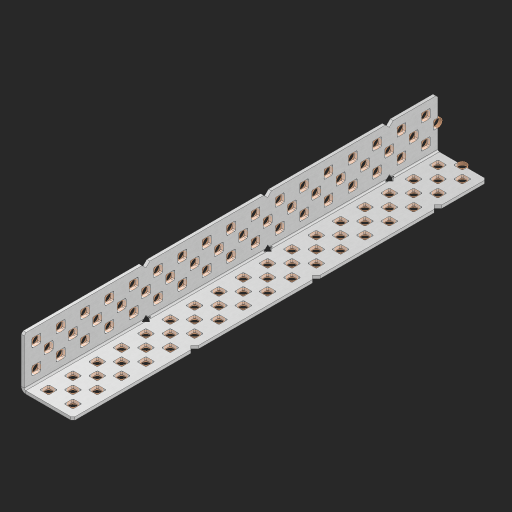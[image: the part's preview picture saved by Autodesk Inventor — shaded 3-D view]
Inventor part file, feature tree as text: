
AUTODESK INVENTOR PART (.ipt)
format: ipt  version: 2023 (Build 270158000, 158)  size: 1,382,912 bytes
history: native  units: in
note: dims shown in document units (in); Inventor stores cm internally (conversion verified against a paired STEP export)
features: other x108, extrude x100, sheet_metal_op x8, sketch x7, pattern_linear x2, mirror x1, chamfer x1
ambient origin geometry x8: Origin, YZ Plane, XZ Plane, XY Plane, X Axis, Y Axis, Z Axis, Center Point
bodies: Solid1 (feature_tree), Body (feature_tree)
feature tree (227):
  sheet_metal_op  "Flanges"
  sheet_metal_op  "Body Pattern"
  pattern_linear  "Center Pattern"  Spacing1=1.0in  [1 undecoded]
  other  "Arc Length"
  pattern_linear  "Notch Pattern"  Spacing1=0.25in  [1 undecoded]
  other  "Diagonal Plane"
  mirror  "Everything Mirrored"
  chamfer  "End Chamfer"
  sketch  "Sketch1"  dims[d0=1.0in]
  other  "Plate1"
  sketch  "Sketch2"  dims[d1=8.5in]
  other  "Plate2"
  sheet_metal_op  "Bend1"
  sheet_metal_op  "Corner1"
  sketch  "Sketch8"  dims[d2=0.0625in]
  sketch  "Sketch9"  dims[d3=0.0625in]
  other  "Srf91"
  sheet_metal_op  "Body Pattern Sketch"
  other  "Srf92"
  sketch  "Sketch13"  dims[d4=0.0312in]
  sketch  "Sketch15"  dims[d5=0.125in]
  sketch  "Sketch16"  dims[d6=0.0625in d7=1.0in d8=90.0deg d9=0.0312in d10=0.25in d11=0.0625in d12=0.0625in d49=0.182in d50=0.02in d52=0.25in d53=0.0625in d54=0.0in d55=0.172in d56=1.0in d57=0.0in d60=6.6929in d62=0.5in d63=0.7874in d65=0.5in d85=0.1473in d86=0.1782in d89=0.0625in d90=0.0in d91=0.04in d92=0.0491in d95=2.5in d96=0.04in d97=0.25in d98=45.0deg d99=0.25in d106=0.182in d107=0.02in d108=0.5in d110=0.0625in d111=0.0in d112=0.172in d113=0.5in d114=0.0in d117=0.5in d123=0.25in d125=0.25in d126=0.0491in d127=0.1473in d128=0.08in d129=0.04in d130=2.5in]
  other  "Srf786"
  other  "Srf856"
  other  "Srf857"
  other  "Srf858"
  other  "Srf859"
  other  "Srf860"
  other  "Srf861"
  other  "Srf889"
  other  "Srf890"
  other  "Srf891"
  other  "Srf1275"
  other  "Srf1276"
  other  "Srf1278"
  other  "Srf1279"
  other  "Srf1280"
  other  "Srf1281"
  other  "Srf1282"
  other  "Srf1283"
  other  "Srf1277"
  other  "Srf1285"
  other  "Srf1286"
  other  "Srf1287"
  other  "Srf1383"
  other  "Srf1384"
  other  "Srf1385"
  other  "Srf1386"
  other  "Srf1387"
  other  "Srf1388"
  other  "Srf1389"
  other  "Srf1390"
  other  "Srf1391"
  other  "Srf1392"
  other  "Srf1393"
  other  "Srf1394"
  other  "Srf1395"
  other  "Srf1396"
  other  "Srf1397"
  other  "Srf1398"
  other  "Srf1399"
  other  "Srf1400"
  other  "Srf1401"
  other  "Srf1402"
  other  "Srf1403"
  other  "Srf1404"
  other  "Srf1405"
  other  "Srf1406"
  other  "Srf1407"
  other  "Srf1408"
  other  "Srf1445"
  other  "Srf1446"
  other  "Srf1447"
  other  "Srf1448"
  other  "Srf1449"
  other  "Srf1450"
  other  "Srf1451"
  other  "Srf1452"
  other  "Srf1453"
  other  "Srf1454"
  other  "Srf1455"
  other  "Srf1456"
  other  "Srf1457"
  other  "Srf1475"
  other  "Srf1476"
  other  "Srf1477"
  other  "Srf1478"
  other  "Srf1479"
  other  "Srf1480"
  other  "Srf1481"
  other  "Srf1482"
  other  "Srf1483"
  other  "Srf1484"
  other  "Srf1485"
  other  "Srf1486"
  other  "Srf1487"
  other  "Srf1488"
  other  "Srf1489"
  other  "Srf1490"
  other  "Srf1491"
  other  "Srf1492"
  other  "Srf1493"
  other  "Srf1494"
  other  "Srf1495"
  other  "Srf1496"
  other  "Srf1497"
  other  "Srf1498"
  other  "Srf1499"
  other  "Srf1500"
  other  "Srf1537"
  other  "Srf1538"
  other  "Srf1539"
  other  "Srf1540"
  other  "Srf1541"
  other  "Srf1542"
  other  "Srf1543"
  other  "Srf1544"
  other  "Srf1545"
  other  "Srf1546"
  other  "Srf1547"
  other  "Srf1548"
  other  "Srf1549"
  sheet_metal_op  "Body Stamp"
  sheet_metal_op  "Body Circle"
  other  "Center Stamp"
  other  "Center Circle"
  sheet_metal_op  "Notch"
  extrude  "ExtrusionSrf92"  Depth=0.0625in
  extrude  "ExtrusionSrf856"  Depth=0.0625in
  extrude  "ExtrusionSrf857"  Depth=0.182in
  extrude  "ExtrusionSrf858"  Depth=0.02in
  extrude  "ExtrusionSrf859"  Depth=0.25in
  extrude  "ExtrusionSrf860"  Depth=0.0625in
  extrude  "ExtrusionSrf861"  TaperAngle=0.0deg  [1 undecoded]
  extrude  "ExtrusionSrf889"  Depth=2.5in
  extrude  "ExtrusionSrf890"  Depth=1.0in TaperAngle=0.0deg
  extrude  "ExtrusionSrf891"  Depth=2.5in
  extrude  "ExtrusionSrf1275"  Depth=0.5in
  extrude  "ExtrusionSrf1276"  Depth=2.5in
  extrude  "ExtrusionSrf1277"  Depth=2.5in
  extrude  "ExtrusionSrf1278"  Depth=0.0625in
  extrude  "ExtrusionSrf1279"  Depth=2.5in TaperAngle=0.0deg
  extrude  "ExtrusionSrf1280"  Depth=2.5in
  extrude  "ExtrusionSrf1281"  Depth=0.25in TaperAngle=45.0deg
  extrude  "ExtrusionSrf1282"  Depth=0.25in
  extrude  "ExtrusionSrf1345"  Depth=0.182in
  extrude  "ExtrusionSrf1346"  Depth=0.02in
  extrude  "ExtrusionSrf1347"  Depth=0.5in
  extrude  "ExtrusionSrf1348"  Depth=0.0625in
  extrude  "ExtrusionSrf1383"  TaperAngle=0.0deg  [1 undecoded]
  extrude  "ExtrusionSrf1384"  Depth=2.5in
  extrude  "ExtrusionSrf1385"  Depth=0.5in TaperAngle=0.0deg
  extrude  "ExtrusionSrf1386"  Depth=0.5in
  extrude  "ExtrusionSrf1387"  Depth=0.25in
  extrude  "ExtrusionSrf1388"  Depth=0.25in
  extrude  "ExtrusionSrf1389"  Depth=2.5in
  extrude  "ExtrusionSrf1390"  Depth=2.5in
  extrude  "ExtrusionSrf1391"  Depth=2.5in
  extrude  "ExtrusionSrf1392"  Depth=2.5in
  extrude  "ExtrusionSrf1393"  Depth=2.5in
  extrude  "ExtrusionSrf1394"  [1 undecoded]
  extrude  "ExtrusionSrf1395"  [1 undecoded]
  extrude  "ExtrusionSrf1396"  [1 undecoded]
  extrude  "ExtrusionSrf1397"  [1 undecoded]
  extrude  "ExtrusionSrf1398"  [1 undecoded]
  extrude  "ExtrusionSrf1399"  [1 undecoded]
  extrude  "ExtrusionSrf1400"  [1 undecoded]
  extrude  "ExtrusionSrf1401"  [1 undecoded]
  extrude  "ExtrusionSrf1402"  [1 undecoded]
  extrude  "ExtrusionSrf1403"  [1 undecoded]
  extrude  "ExtrusionSrf1404"  [1 undecoded]
  extrude  "ExtrusionSrf1405"  [1 undecoded]
  extrude  "ExtrusionSrf1406"  [1 undecoded]
  extrude  "ExtrusionSrf1407"  [1 undecoded]
  extrude  "ExtrusionSrf1408"  [1 undecoded]
  extrude  "ExtrusionSrf1445"  [1 undecoded]
  extrude  "ExtrusionSrf1446"  [1 undecoded]
  extrude  "ExtrusionSrf1447"  [1 undecoded]
  extrude  "ExtrusionSrf1448"  [1 undecoded]
  extrude  "ExtrusionSrf1449"  [1 undecoded]
  extrude  "ExtrusionSrf1450"  [1 undecoded]
  extrude  "ExtrusionSrf1451"  [1 undecoded]
  extrude  "ExtrusionSrf1452"  [1 undecoded]
  extrude  "ExtrusionSrf1453"  [1 undecoded]
  extrude  "ExtrusionSrf1454"  [1 undecoded]
  extrude  "ExtrusionSrf1455"  [1 undecoded]
  extrude  "ExtrusionSrf1456"  [1 undecoded]
  extrude  "ExtrusionSrf1457"  [1 undecoded]
  extrude  "ExtrusionSrf1475"  [1 undecoded]
  extrude  "ExtrusionSrf1476"  [1 undecoded]
  extrude  "ExtrusionSrf1477"  [1 undecoded]
  extrude  "ExtrusionSrf1478"  [1 undecoded]
  extrude  "ExtrusionSrf1479"  [1 undecoded]
  extrude  "ExtrusionSrf1480"  [1 undecoded]
  extrude  "ExtrusionSrf1481"  [1 undecoded]
  extrude  "ExtrusionSrf1482"  [1 undecoded]
  extrude  "ExtrusionSrf1483"  [1 undecoded]
  extrude  "ExtrusionSrf1484"  [1 undecoded]
  extrude  "ExtrusionSrf1485"  [1 undecoded]
  extrude  "ExtrusionSrf1486"  [1 undecoded]
  extrude  "ExtrusionSrf1487"  [1 undecoded]
  extrude  "ExtrusionSrf1488"  [1 undecoded]
  extrude  "ExtrusionSrf1489"  [1 undecoded]
  extrude  "ExtrusionSrf1490"  [1 undecoded]
  extrude  "ExtrusionSrf1491"  [1 undecoded]
  extrude  "ExtrusionSrf1492"  [1 undecoded]
  extrude  "ExtrusionSrf1493"  [1 undecoded]
  extrude  "ExtrusionSrf1494"  [1 undecoded]
  extrude  "ExtrusionSrf1495"  [1 undecoded]
  extrude  "ExtrusionSrf1496"  [1 undecoded]
  extrude  "ExtrusionSrf1497"  [1 undecoded]
  extrude  "ExtrusionSrf1498"  [1 undecoded]
  extrude  "ExtrusionSrf1499"  [1 undecoded]
  extrude  "ExtrusionSrf1500"  [1 undecoded]
  extrude  "ExtrusionSrf1537"  [1 undecoded]
  extrude  "ExtrusionSrf1538"  [1 undecoded]
  extrude  "ExtrusionSrf1539"  [1 undecoded]
  extrude  "ExtrusionSrf1540"  [1 undecoded]
  extrude  "ExtrusionSrf1541"  [1 undecoded]
  extrude  "ExtrusionSrf1542"  [1 undecoded]
  extrude  "ExtrusionSrf1543"  [1 undecoded]
  extrude  "ExtrusionSrf1544"  [1 undecoded]
  extrude  "ExtrusionSrf1545"  [1 undecoded]
  extrude  "ExtrusionSrf1546"  [1 undecoded]
  extrude  "ExtrusionSrf1547"  [1 undecoded]
  extrude  "ExtrusionSrf1548"  [1 undecoded]
  extrude  "ExtrusionSrf1549"  [1 undecoded]
note: 71 required parameter values undecoded (feature->parameter linkage not recoverable at this tier; creation-order binding heuristic only, values carry confidence <= 0.55)
